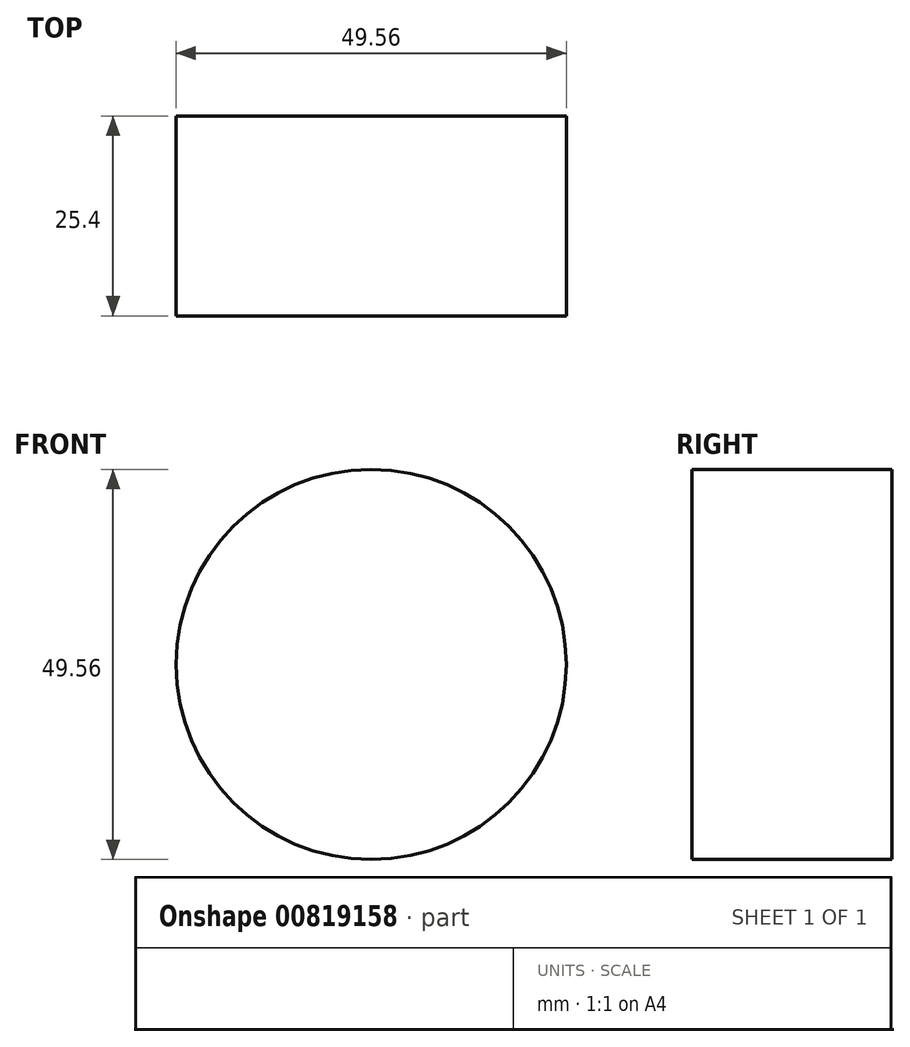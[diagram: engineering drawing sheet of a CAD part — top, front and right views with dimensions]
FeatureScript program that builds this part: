
annotation { "Feature Type Name" : "Feature", "Feature Type Description" : "" }
export const myFeature = defineFeature(function(context is Context, id is Id, definition is map)
    precondition{}
    {
        {
            var Q0;
            Q0=qCreatedBy(makeId("Front.planeOp"),FACE);
            var sketch = newSketch(context, id + "F0", { "sketchPlane" : qUnion([Q0])});
            skCircle(sketch, "E0", {"center": v(0, 0) * mm, "radius": 14.85 * mm});
            skCircle(sketch, "E1", {"center": v(0, 0) * mm, "radius": 21.45 * mm});
            skCircle(sketch, "E2", {"center": v(0, 0) * mm, "radius": 24.78 * mm});
            skSolve(sketch);
        }
        {
            var Q0;
            Q0 = qSketchRegion(id + "F0", true);
            var Q1;
            Q1=makeQuery(id+"F0.imprint","IMPRINT",FACE,{"disambiguationData":[TD([[makeQuery(id+"F0.imprint","IMPRINT",EDGE,{"derivedFrom":sQuery(id+"F0.wireOp",EDGE,"E0")}),1.0]])]});
            var Q2;
            Q2=makeQuery(id+"F0.imprint","IMPRINT",FACE,{"disambiguationData":[TD([[makeQuery(id+"F0.imprint","IMPRINT",EDGE,{"derivedFrom":sQuery(id+"F0.wireOp",EDGE,"E0")}),-1.0]])]});
            extrude(context, id + "F1", {"entities" : qUnion([Q0, Q1, Q2]), "depth" : 25.4 * mm, "offsetDistance" : 25.4 * mm});
        }
    });
